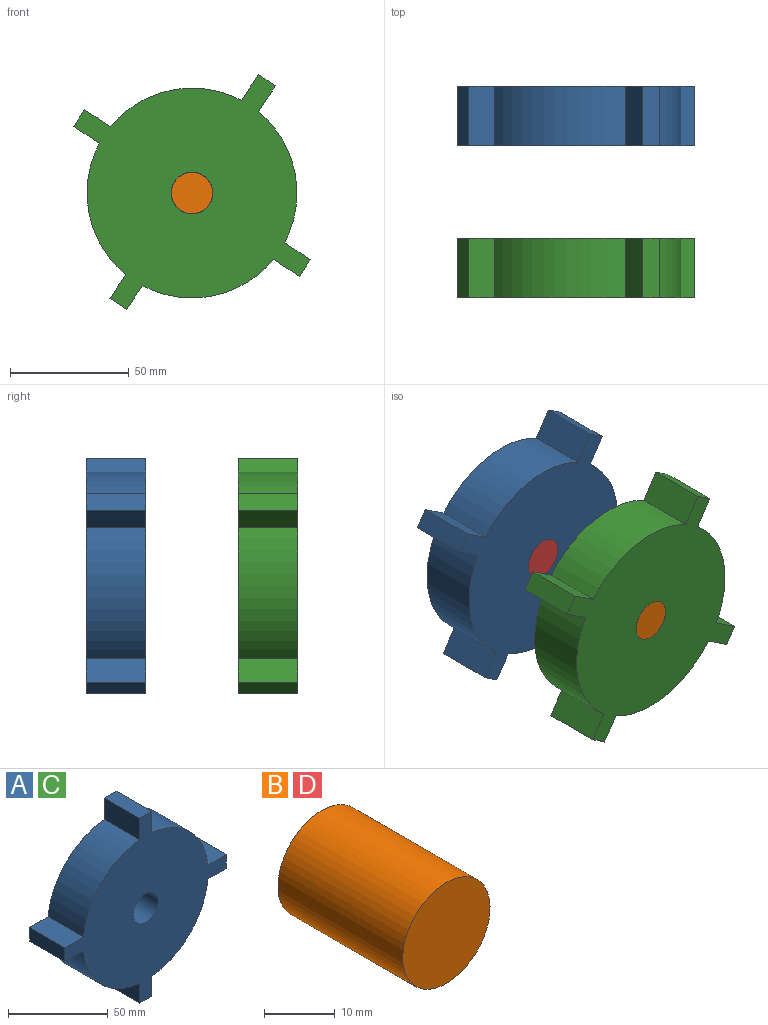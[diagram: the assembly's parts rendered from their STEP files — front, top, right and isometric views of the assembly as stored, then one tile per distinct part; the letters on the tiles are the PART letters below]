
ASSEMBLY  parts=4 mates=3
PART A: 19 faces, bbox 114.2x25x113.2 mm
  f0: plane 25x12.08mm, normal (1,0,0), area 301.9mm2, adj f1,f15,f16,f17
  f1: cylinder r=44.21mm len=39.81mm, axis (0,1,0), area 1525.6mm2, adj f0,f2,f16,f17
  f2: plane 25x13.08mm, normal (0,0,-1), area 327mm2, adj f1,f3,f16,f17
  f3: plane 25x8.4mm, normal (1,0,0), area 210.1mm2, adj f2,f4,f16,f17
  f4: plane 25x13.08mm, normal (0,0,1), area 327mm2, adj f3,f5,f16,f17
  f5: cylinder r=44.21mm len=39.8mm, axis (0,1,0), area 1523.2mm2, adj f4,f6,f16,f17
  f6: plane 25x13.08mm, normal (1,0,0), area 327mm2, adj f5,f7,f16,f17
  f7: plane 25x8.59mm, normal (0,0,1), area 214.9mm2, adj f6,f8,f16,f17
  f8: plane 25x13.08mm, normal (-1,0,0), area 327mm2, adj f7,f9,f16,f17
  f9: cylinder r=44.21mm len=39.8mm, axis (0,1,0), area 1523.2mm2, adj f8,f10,f16,f17
  f10: plane 25x13.08mm, normal (0,0,1), area 327mm2, adj f9,f11,f16,f17
  f11: plane 25x8.4mm, normal (-1,0,0), area 210.1mm2, adj f10,f12,f16,f17
  f12: plane 25x13.08mm, normal (0,0,-1), area 327mm2, adj f11,f13,f16,f17
  f13: cylinder r=44.21mm len=39.81mm, axis (0,1,0), area 1525.6mm2, adj f12,f14,f16,f17
  f14: plane 25x12.08mm, normal (-1,0,0), area 301.9mm2, adj f13,f15,f16,f17
  f15: plane 25x8.4mm, normal (0,0,-1), area 210.1mm2, adj f0,f14,f16,f17
  f16: plane 114.17x113.16mm, normal (0,-1,0), area 6328.5mm2, adj f0,f1,f2,f3,f4,f5,f6,f7
  f17: plane 114.17x113.16mm, normal (0,1,0), area 6328.5mm2, adj f0,f1,f2,f3,f4,f5,f6,f7
  f18: cylinder r=8.75mm len=25mm, axis (0,1,0), area 1374.4mm2, adj f16,f17
PART B: 3 faces, bbox 17.5x25x17.5 mm
  f0: cylinder r=8.75mm len=25mm, axis (0,1,0), area 1374.4mm2, adj f1,f2
  f1: plane 17.5x17.5mm, normal (0,-1,0), area 240.5mm2, adj f0
  f2: plane 17.5x17.5mm, normal (0,1,0), area 240.5mm2, adj f0
PART C: same geometry as A
PART D: same geometry as B
PLACE A rot(axis=(0,1,0),33.6deg) t=(132.2,39.1,0)mm
PLACE B t=(132.2,0,0)mm fixed
PLACE C rot(axis=(0.29,0,0.96),180deg) t=(132.2,-50,0)mm
PLACE D rot(axis=(0,-1,0),100.9deg) t=(132.2,64.1,0)mm
MATE slider A.f1 <-> C.f1  axis (0,1,0) through (132.2,14.1,0)mm
MATE revolute C.f1 <-> B.f0  axis (0,-1,0) through (132.2,-50,0)mm
MATE revolute A.f1 <-> D.f0  axis (0,1,0) through (132.2,14.1,0)mm
